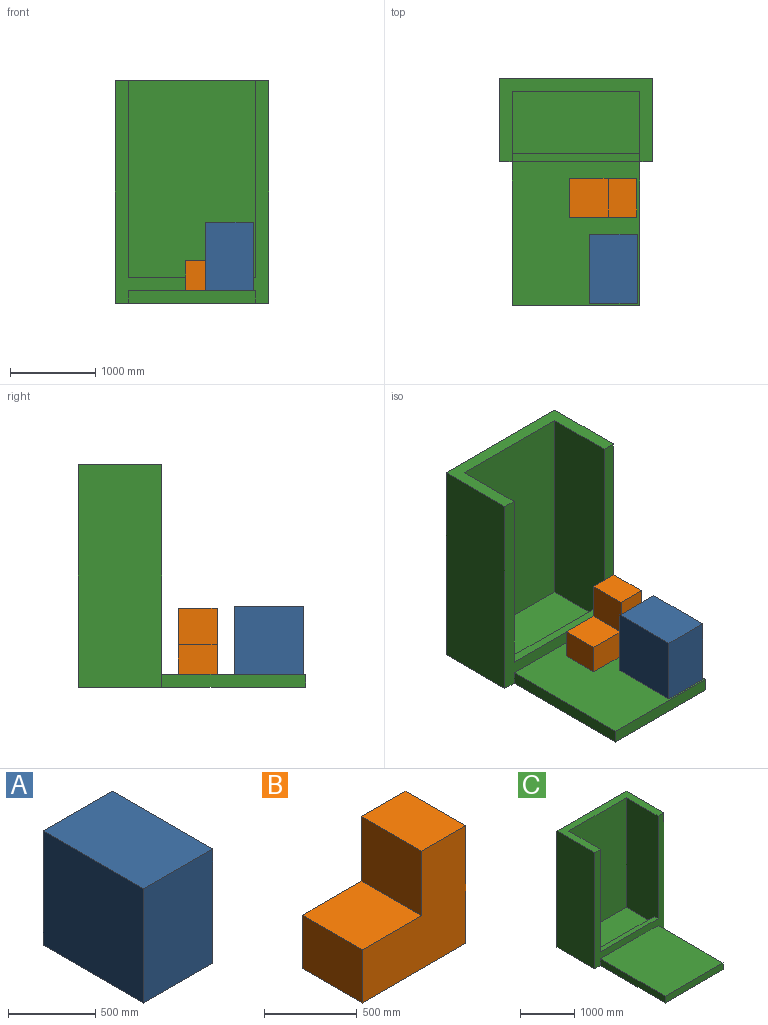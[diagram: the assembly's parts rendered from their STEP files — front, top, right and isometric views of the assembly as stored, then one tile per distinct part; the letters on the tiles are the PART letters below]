
ASSEMBLY  parts=3 mates=2
PART A: 6 faces, bbox 558.8x812.8x800.1 mm
  f0: plane 800.1x558.8mm, normal (0,-1,0), area 447095.9mm2, adj f1,f3,f4,f5
  f1: plane 812.8x800.1mm, normal (1,0,0), area 650321.3mm2, adj f0,f2,f4,f5
  f2: plane 800.1x558.8mm, normal (0,1,0), area 447095.9mm2, adj f1,f3,f4,f5
  f3: plane 812.8x800.1mm, normal (-1,0,0), area 650321.3mm2, adj f0,f2,f4,f5
  f4: plane 812.8x558.8mm, normal (0,0,1), area 454192.6mm2, adj f0,f1,f2,f3
  f5: plane 812.8x558.8mm, normal (0,0,-1), area 454192.6mm2, adj f0,f1,f2,f3
PART B: 8 faces, bbox 787.4x457.2x774.7 mm
  f0: plane 457.2x335.67mm, normal (0,0,1), area 153467.4mm2, adj f1,f2,f3,f7
  f1: plane 787.4x774.7mm, normal (0,-1,0), area 418036.3mm2, adj f0,f2,f4,f5,f6,f7
  f2: plane 774.7x457.2mm, normal (1,0,0), area 354192.8mm2, adj f0,f1,f3,f5
  f3: plane 787.4x774.7mm, normal (0,1,0), area 418036.3mm2, adj f0,f2,f4,f5,f6,f7
  f4: plane 457.2x349.75mm, normal (-1,0,0), area 159906.8mm2, adj f1,f3,f5,f6
  f5: plane 787.4x457.2mm, normal (0,0,-1), area 359999.3mm2, adj f1,f2,f3,f4
  f6: plane 457.2x451.73mm, normal (0,0,1), area 206531.9mm2, adj f1,f3,f4,f7
  f7: plane 457.2x424.95mm, normal (-1,0,0), area 194286.1mm2, adj f0,f1,f3,f6
PART C: 16 faces, bbox 1803.4x2667x2616.2 mm
  f0: plane 1689.1x152.4mm, normal (1,0,0), area 257418.8mm2, adj f3,f4,f5,f7
  f1: plane 1689.1x152.4mm, normal (-1,0,0), area 257418.8mm2, adj f3,f4,f5,f7
  f2: plane 1498.6x723.9mm, normal (0,0,1), area 1084836.5mm2, adj f6,f9,f12,f14
  f3: plane 1498.6x152.4mm, normal (0,-1,0), area 228386.6mm2, adj f0,f1,f4,f5
  f4: plane 1689.1x1498.6mm, normal (0,0,1), area 2531285.3mm2, adj f0,f1,f3,f7
  f5: plane 2667x1803.4mm, normal (0,0,-1), area 4294830.1mm2, adj f0,f1,f3,f7,f11,f13,f15
  f6: plane 1498.6x152.4mm, normal (0,1,0), area 228386.6mm2, adj f2,f8,f12,f14
  f7: plane 2616.2x1803.4mm, normal (0,-1,0), area 1025804.4mm2, adj f0,f1,f4,f5,f8,f10,f12,f13
  f8: plane 1498.6x101.6mm, normal (0,0,1), area 152257.8mm2, adj f6,f7,f12,f14
  f9: plane 2463.8x1498.6mm, normal (0,-1,0), area 3692250.7mm2, adj f2,f10,f12,f14
  f10: plane 1803.4x977.9mm, normal (0,0,1), area 526450.6mm2, adj f7,f9,f11,f12,f13,f14,f15
  f11: plane 2616.2x1803.4mm, normal (0,1,0), area 4718055.1mm2, adj f5,f10,f13,f15
  f12: plane 2463.8x825.5mm, normal (1,0,0), area 2018383.1mm2, adj f2,f6,f7,f8,f9,f10
  f13: plane 2616.2x977.9mm, normal (-1,0,0), area 2558382mm2, adj f5,f7,f10,f11
  f14: plane 2463.8x825.5mm, normal (-1,0,0), area 2018383.1mm2, adj f2,f6,f7,f8,f9,f10
  f15: plane 2616.2x977.9mm, normal (1,0,0), area 2558382mm2, adj f5,f7,f10,f11
PLACE A t=(-918.11,-1233.95,-65.04)mm
PLACE B t=(-924.97,-1212.48,-65.04)mm
PLACE C t=(-887.73,-1260.27,-65.04)mm fixed
MATE planar C.f4 <-> B.f5  axis (0,0,1) through (-887.73,-1673.02,87.36)mm
MATE planar C.f4 <-> A.f5  axis (0,0,1) through (-887.73,-1673.02,87.36)mm
